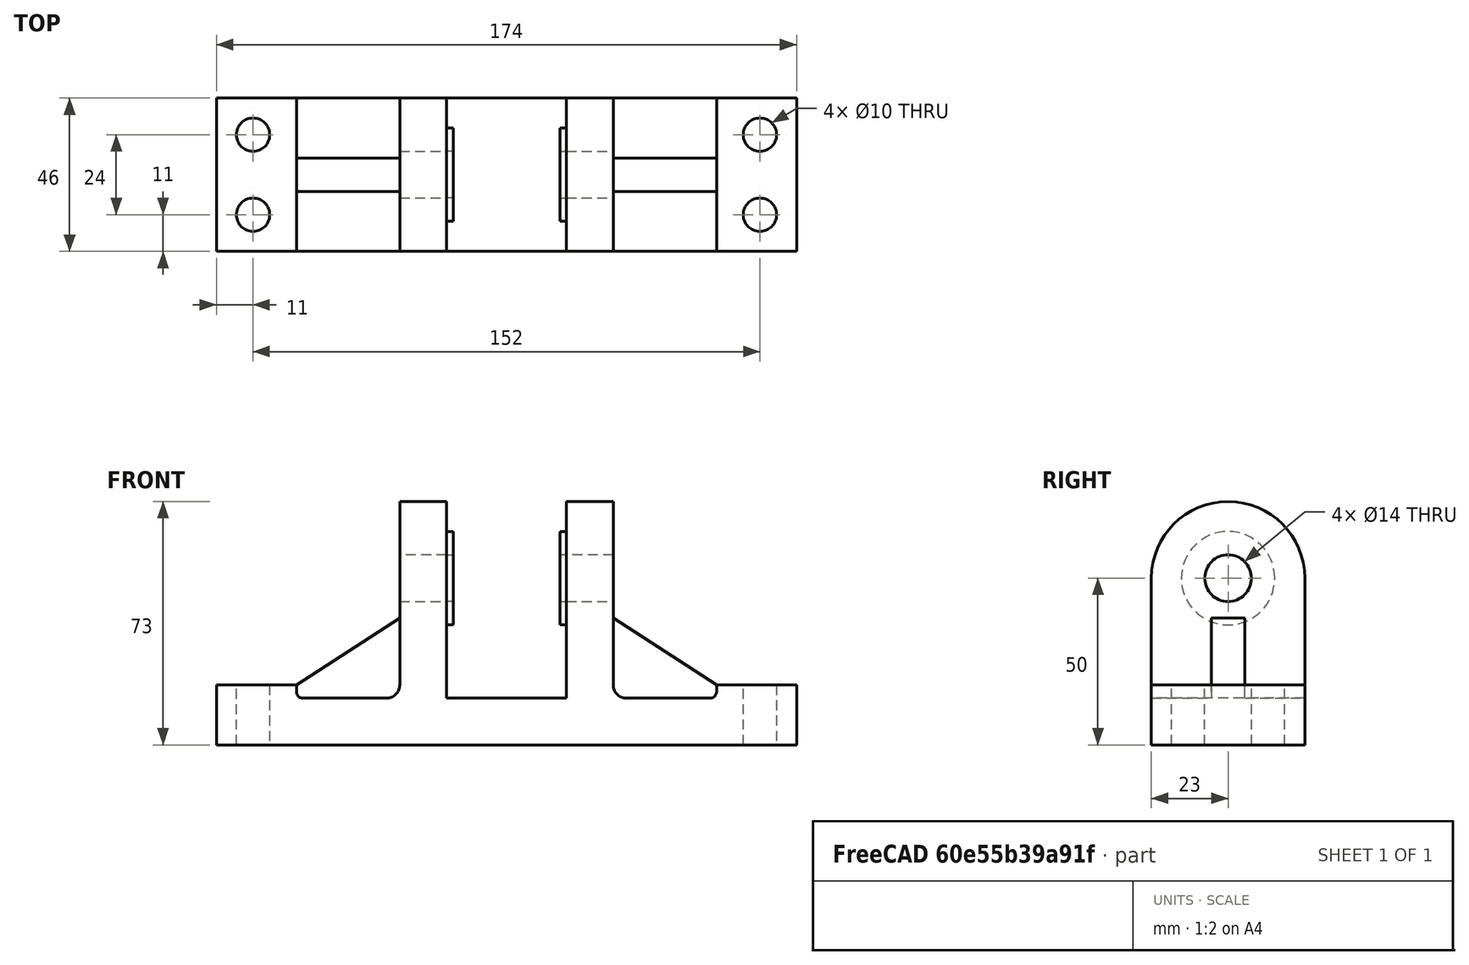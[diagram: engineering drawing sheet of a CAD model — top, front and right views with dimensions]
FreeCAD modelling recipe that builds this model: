
FCSTD DOCUMENT  (FreeCAD 0.21R33771 (Git))
Label: item_04_part_01
License: All rights reserved
LicenseURL: http://en.wikipedia.org/wiki/All_rights_reserved
objects: TechDraw::DrawViewDimension×17, Sketcher::SketchObject×9, PartDesign::Pad×5, PartDesign::Pocket×4, TechDraw::DrawProjGroupItem×3, PartDesign::Mirrored×2, PartDesign::Fillet×2, PartDesign::Body×1, TechDraw::DrawSVGTemplate×1, TechDraw::DrawViewPart×1, TechDraw::DrawProjGroup×1, TechDraw::DrawPage×1
note: 58 computed .brp shape members not serialized (recipe doc carries the construction recipe); baked Part::Feature solids carry a one-line shape summary decoded from their .brp

FEATURE [Sketcher::SketchObject] Sketch
  FullyConstrained = true
  MapMode = 5
  Placement = pos=(0,0,0) rot=(1,0,0;1.5708rad)
  Support = -> [XZ_Plane]
  sketch-geometry (5):
    g0: LineSegment StartX=-87 StartY=9 StartZ=0 EndX=-87 EndY=-9 EndZ=0
    g1: LineSegment StartX=-87 StartY=-9 StartZ=0 EndX=87 EndY=-9 EndZ=0
    g2: LineSegment StartX=87 StartY=-9 StartZ=0 EndX=87 EndY=9 EndZ=0
    g3: LineSegment StartX=87 StartY=9 StartZ=0 EndX=-87 EndY=9 EndZ=0
    g4: GeomPoint X=0 Y=0 Z=0
  constraints (12):
    c: Coincident(g0,g1)
    c: Coincident(g1,g2)
    c: Coincident(g2,g3)
    c: Coincident(g3,g0)
    c: Horizontal(g1)
    c: Horizontal(g3)
    c: Vertical(g0)
    c: Vertical(g2)
    c: Symmetric(g1,g0,g4)
    c: Coincident(g4,g-1)
    c: DistanceX(g3,g3) = 174
    c: DistanceY(g0,g0) = 18
FEATURE [PartDesign::Pad] Pad
  Direction = (0,-1,2e-16)
  Length = 46
  Length2 = 10
  Midplane = true
  Placement = pos=(0,0,0) rot=(1,0,0;1.5708rad)
  Profile = -> Sketch
  ReferenceAxis = -> Sketch [N_Axis]
  Type = 0
FEATURE [Sketcher::SketchObject] Sketch001
  ExternalGeometry = -> [Pad]
  FullyConstrained = false
  MapMode = 5
  Placement = pos=(0,0,0) rot=(1,0,0;1.5708rad)
  Support = -> [XZ_Plane]
  sketch-geometry (4):
    g0: LineSegment StartX=-63 StartY=5 StartZ=0 EndX=63 EndY=5 EndZ=0
    g1: LineSegment StartX=63 StartY=5 StartZ=0 EndX=63 EndY=36.0342 EndZ=0
    g2: LineSegment StartX=63 StartY=36.0342 StartZ=0 EndX=-63 EndY=36.0342 EndZ=0
    g3: LineSegment StartX=-63 StartY=36.0342 StartZ=0 EndX=-63 EndY=5 EndZ=0
  constraints (11):
    c: Coincident(g0,g1)
    c: Coincident(g1,g2)
    c: Coincident(g2,g3)
    c: Coincident(g3,g0)
    c: Horizontal(g0)
    c: Horizontal(g2)
    c: Vertical(g1)
    c: Vertical(g3)
    c: DistanceX(g2,g2) = 126
    c: DistanceX(g-3,g0) = 24
    c: DistanceY(g0,g-3) = 4
FEATURE [PartDesign::Pocket] Pocket
  AlongSketchNormal = false
  BaseFeature = -> Pad
  Direction = (0,1,-2e-16)
  Length = 50
  Length2 = 5
  Midplane = true
  Placement = pos=(0,0,0) rot=(1,0,0;1.5708rad)
  Profile = -> Sketch001
  ReferenceAxis = -> Sketch001 [N_Axis]
  Type = 0
FEATURE [Sketcher::SketchObject] Sketch002
  ExternalGeometry = -> [Pocket]
  FullyConstrained = true
  MapMode = 5
  Placement = pos=(0,0,0) rot=(1,0,0;1.5708rad)
  Support = -> [XZ_Plane]
  sketch-geometry (4):
    g0: LineSegment StartX=-32 StartY=-9 StartZ=0 EndX=-18 EndY=-9 EndZ=0
    g1: LineSegment StartX=-18 StartY=-9 StartZ=0 EndX=-18 EndY=64 EndZ=0
    g2: LineSegment StartX=-18 StartY=64 StartZ=0 EndX=-32 EndY=64 EndZ=0
    g3: LineSegment StartX=-32 StartY=64 StartZ=0 EndX=-32 EndY=-9 EndZ=0
  constraints (12):
    c: Coincident(g0,g1)
    c: Coincident(g1,g2)
    c: Coincident(g2,g3)
    c: Coincident(g3,g0)
    c: Horizontal(g0)
    c: Horizontal(g2)
    c: Vertical(g1)
    c: Vertical(g3)
    c: DistanceX(g-4,g0) = 55
    c: DistanceX(g2,g2) = 14
    c: DistanceY(g1,g1) = 73
    c: PointOnObject(g-6,g0)
FEATURE [PartDesign::Pad] Pad001
  BaseFeature = -> Pocket
  Direction = (0,-1,2e-16)
  Length = 46
  Length2 = 10
  Midplane = true
  Placement = pos=(0,0,0) rot=(1,0,0;1.5708rad)
  Profile = -> Sketch002
  ReferenceAxis = -> Sketch002 [N_Axis]
  Refine = true
  Type = 0
FEATURE [Sketcher::SketchObject] Sketch003
  ExternalGeometry = -> [Pad001]
  FullyConstrained = false
  MapMode = 5
  Placement = pos=(0,0,0) rot=(1,0,0;1.5708rad)
  Support = -> [XZ_Plane]
  sketch-geometry (4):
    g0: LineSegment StartX=18 StartY=-9 StartZ=0 EndX=32 EndY=-9 EndZ=0
    g1: LineSegment StartX=32 StartY=-9 StartZ=0 EndX=32 EndY=64 EndZ=0
    g2: LineSegment StartX=32 StartY=64 StartZ=0 EndX=18 EndY=64 EndZ=0
    g3: LineSegment StartX=18 StartY=64 StartZ=0 EndX=18 EndY=-9 EndZ=0
  constraints (10):
    c: Coincident(g0,g1)
    c: Coincident(g1,g2)
    c: Coincident(g2,g3)
    c: Coincident(g3,g0)
    c: Horizontal(g0)
    c: Horizontal(g2)
    c: Vertical(g1)
    c: Vertical(g3)
    c: DistanceX(g2,g2) = 14
    c: DistanceY(g1,g1) = 73
FEATURE [PartDesign::Pad] Pad002
  BaseFeature = -> Pad001
  Direction = (0,-1,2e-16)
  Length = 46
  Length2 = 10
  Midplane = true
  Placement = pos=(0,0,0) rot=(1,0,0;1.5708rad)
  Profile = -> Sketch003
  ReferenceAxis = -> Sketch003 [N_Axis]
  Refine = true
  Type = 0
FEATURE [Sketcher::SketchObject] Sketch004
  ExternalGeometry = -> [Pad002]
  FullyConstrained = true
  MapMode = 5
  Support = -> [XY_Plane]
  sketch-geometry (4):
    g0: Circle CenterX=-76 CenterY=12 CenterZ=0 NormalX=0 NormalY=0 NormalZ=1 AngleXU=0 Radius=5
    g1: Circle CenterX=-76 CenterY=-12 CenterZ=0 NormalX=0 NormalY=0 NormalZ=1 AngleXU=0 Radius=5
    g2: Circle CenterX=76 CenterY=12 CenterZ=0 NormalX=0 NormalY=0 NormalZ=1 AngleXU=0 Radius=5
    g3: Circle CenterX=76 CenterY=-12 CenterZ=0 NormalX=0 NormalY=0 NormalZ=1 AngleXU=0 Radius=5
  constraints (12):
    c: Equal(g0,g1)
    c: Equal(g1,g3)
    c: Equal(g3,g2)
    c: Diameter(g0) = 10
    c: Vertical(g0,g1)
    c: Vertical(g2,g3)
    c: Horizontal(g2,g0)
    c: Horizontal(g1,g3)
    c: DistanceY(g0,g-4) = 11
    c: DistanceX(g-4,g0) = 11
    c: DistanceY(g-6,g3) = 11
    c: DistanceX(g3,g-6) = 11
FEATURE [PartDesign::Pocket] Pocket001
  BaseFeature = -> Pad002
  Direction = (0,0,-1)
  Length = 5
  Length2 = 5
  Midplane = true
  Placement = pos=(0,0,0) rot=(1,0,0;1.5708rad)
  Profile = -> Sketch004
  ReferenceAxis = -> Sketch004 [N_Axis]
  Type = 1
FEATURE [Sketcher::SketchObject] Sketch005
  ExternalGeometry = -> [Pocket001]
  FullyConstrained = false
  MapMode = 5
  Placement = pos=(0,0,0) rot=(0.57735,0.57735,0.57735;2.0944rad)
  Support = -> [YZ_Plane]
  sketch-geometry (4):
    g0: ArcOfCircle CenterX=0 CenterY=41 CenterZ=0 NormalX=0 NormalY=0 NormalZ=1 AngleXU=0 Radius=23 StartAngle=1e-16 EndAngle=3.14159
    g1: LineSegment StartX=-23 StartY=64 StartZ=0 EndX=23 EndY=64 EndZ=0
    g2: LineSegment StartX=23 StartY=64 StartZ=0 EndX=23 EndY=41 EndZ=0
    g3: LineSegment StartX=-23 StartY=41 StartZ=0 EndX=-23 EndY=64 EndZ=0
  constraints (10):
    c: PointOnObject(g0,g-2)
    c: Diameter(g0) = 46
    c: DistanceY(g-3,g0) = 50
    c: Coincident(g1,g2)
    c: Coincident(g3,g1)
    c: Horizontal(g1)
    c: Vertical(g2)
    c: Vertical(g3)
    c: Coincident(g1,g-6)
    c: PointOnObject(g-5,g2)
FEATURE [PartDesign::Pocket] Pocket002
  BaseFeature = -> Pocket001
  Direction = (-1,2e-16,-3e-16)
  Length = 5
  Length2 = 5
  Midplane = true
  Placement = pos=(0,0,0) rot=(1,0,0;1.5708rad)
  Profile = -> Sketch005
  ReferenceAxis = -> Sketch005 [N_Axis]
  Type = 1
FEATURE [Sketcher::SketchObject] Sketch006
  ExternalGeometry = -> [Pocket002]
  FullyConstrained = true
  MapMode = 5
  Placement = pos=(32,0,0) rot=(0.707107,0,0.707107;3.14159rad)
  Support = -> [Pocket002]
  sketch-geometry (1):
    g0: Circle CenterX=41 CenterY=0 CenterZ=0 NormalX=0 NormalY=0 NormalZ=1 AngleXU=0 Radius=7
  constraints (3):
    c: DistanceX(g-3,g0) = 50
    c: PointOnObject(g0,g-1)
    c: Diameter(g0) = 14
FEATURE [PartDesign::Pocket] Pocket003
  BaseFeature = -> Pocket002
  Direction = (-1,0,2e-16)
  Length = 5
  Length2 = 5
  Placement = pos=(0,0,0) rot=(1,0,0;1.5708rad)
  Profile = -> Sketch006
  ReferenceAxis = -> Sketch006 [N_Axis]
  Type = 1
FEATURE [Sketcher::SketchObject] Sketch007
  ExternalGeometry = -> [Pocket003]
  FullyConstrained = true
  MapMode = 5
  Placement = pos=(-18,0,0) rot=(0.707107,0,0.707107;3.14159rad)
  Support = -> [Pocket003]
  sketch-geometry (2):
    g0: Circle CenterX=41 CenterY=0 CenterZ=0 NormalX=0 NormalY=0 NormalZ=1 AngleXU=0 Radius=7
    g1: Circle CenterX=41 CenterY=0 CenterZ=0 NormalX=0 NormalY=0 NormalZ=1 AngleXU=0 Radius=14
  constraints (5):
    c: PointOnObject(g0,g-1)
    c: Coincident(g1,g0)
    c: Diameter(g0) = 14
    c: Diameter(g1) = 28
    c: DistanceX(g-3,g0) = 50
FEATURE [PartDesign::Pad] Pad003
  BaseFeature = -> Pocket003
  Direction = (1,0,-2e-16)
  Length = 2
  Length2 = 10
  Placement = pos=(0,0,0) rot=(1,0,0;1.5708rad)
  Profile = -> Sketch007
  ReferenceAxis = -> Sketch007 [N_Axis]
  Type = 0
FEATURE [PartDesign::Mirrored] Mirrored
  BaseFeature = -> Pad003
  MirrorPlane = -> YZ_Plane
  Originals = -> [Pad003]
  Placement = pos=(0,0,0) rot=(1,0,0;1.5708rad)
FEATURE [Sketcher::SketchObject] Sketch008
  ExternalGeometry = -> [Mirrored]
  FullyConstrained = true
  MapMode = 5
  Placement = pos=(0,0,0) rot=(1,0,0;1.5708rad)
  Support = -> [XZ_Plane]
  sketch-geometry (4):
    g0: LineSegment StartX=32 StartY=29 StartZ=0 EndX=32 EndY=5 EndZ=0
    g1: LineSegment StartX=32 StartY=5 StartZ=0 EndX=63 EndY=5 EndZ=0
    g2: LineSegment StartX=63 StartY=5 StartZ=0 EndX=63 EndY=9 EndZ=0
    g3: LineSegment StartX=63 StartY=9 StartZ=0 EndX=32 EndY=29 EndZ=0
  constraints (9):
    c: Coincident(g0,g-4)
    c: Coincident(g0,g1)
    c: Coincident(g1,g-6)
    c: PointOnObject(g0,g-4)
    c: DistanceY(g0,g-5) = 12
    c: Coincident(g1,g2)
    c: Coincident(g2,g-7)
    c: Coincident(g2,g3)
    c: Coincident(g3,g0)
FEATURE [PartDesign::Pad] Pad004
  BaseFeature = -> Mirrored
  Direction = (0,-1,2e-16)
  Length = 10
  Length2 = 10
  Midplane = true
  Placement = pos=(0,0,0) rot=(1,0,0;1.5708rad)
  Profile = -> Sketch008
  ReferenceAxis = -> Sketch008 [N_Axis]
  Type = 0
FEATURE [PartDesign::Mirrored] Mirrored001
  BaseFeature = -> Pad004
  MirrorPlane = -> Sketch008 [V_Axis]
  Originals = -> [Pad004]
  Placement = pos=(0,0,0) rot=(1,0,0;1.5708rad)
FEATURE [PartDesign::Fillet] Fillet
  Base = -> Mirrored001 [Edge68,Edge64,Edge87,Edge84]
  BaseFeature = -> Mirrored001
  Placement = pos=(0,0,0) rot=(1,0,0;1.5708rad)
  Radius = 4
  SupportTransform = false
  UseAllEdges = false
FEATURE [PartDesign::Fillet] Fillet001
  Base = -> Fillet [Edge70,Edge108,Edge99,Edge20]
  BaseFeature = -> Fillet
  Placement = pos=(0,0,0) rot=(1,0,0;1.5708rad)
  Radius = 2
  SupportTransform = false
  UseAllEdges = false
FEATURE [PartDesign::Body] Body
  Group = -> [Sketch,Pad,Sketch001,Pocket,Sketch002,Pad001,Sketch003,Pad002,Sketch004,Pocket001,Sketch005,Pocket002,Sketch006,Pocket003,Sketch007,Pad003,Mirrored,Sketch008,Pad004,Mirrored001,Fillet,Fillet001]
  Origin = -> Origin
  Tip = -> Fillet001
FEATURE [TechDraw::DrawSVGTemplate] Template
  EditableTexts = Designed_by_Name=Reza Heshmati; Drawing_number=Drawing number; FC-Date=Date; FC-SC=Scale; FC-SH=Sheet; FC-Title=Item #4 (part 1); Subtitle=Subtitle; Weight=Weight
  Height = 210
  Orientation = 1
  Template = <path>
  Width = 297
FEATURE [TechDraw::DrawViewPart] View
  Caption = 3D View
  CoarseView = false
  Direction = (0.57735,-0.57735,0.57735)
  Focus = 100
  HardHidden = false
  IsoCount = 0
  IsoHidden = false
  IsoVisible = false
  LockPosition = false
  Perspective = false
  Rotation = 0
  Scale = 0.5
  ScaleType = 2
  ScrubCount = 0
  SeamHidden = false
  SeamVisible = false
  SmoothHidden = false
  SmoothVisible = true
  Source = -> [Fillet001]
  X = 74.4732
  XDirection = (0.707107,0.707107,0)
  Y = 153.079
FEATURE [TechDraw::DrawProjGroupItem] ProjItem  label="Side View"
  Caption = Side View
  CoarseView = false
  Direction = (0,-1,0)
  Focus = 100
  HardHidden = false
  IsoCount = 0
  IsoHidden = false
  IsoVisible = false
  LockPosition = true
  Perspective = false
  Rotation = 0
  RotationVector = (1,0,0)
  Scale = 0.5
  ScaleType = 2
  ScrubCount = 0
  SeamHidden = false
  SeamVisible = false
  SmoothHidden = false
  SmoothVisible = true
  Source = -> [Fillet001]
  Type = 0
  X = 0
  XDirection = (1,0,0)
  Y = 0
FEATURE [TechDraw::DrawProjGroupItem] ProjItem001  label="Front View"
  Caption = Front View
  CoarseView = false
  Direction = (1,-1e-16,0)
  Focus = 100
  HardHidden = false
  IsoCount = 0
  IsoHidden = false
  IsoVisible = false
  LockPosition = false
  Perspective = false
  Rotation = 0
  RotationVector = (1,0,0)
  Scale = 0.5
  ScaleType = 2
  ScrubCount = 0
  SeamHidden = false
  SeamVisible = false
  SmoothHidden = false
  SmoothVisible = true
  Source = -> [Fillet001]
  Type = 2
  X = -85
  XDirection = (1e-16,1,0)
  Y = 0
FEATURE [TechDraw::DrawProjGroupItem] ProjItem002  label="Bottom View"
  Caption = Bottom View
  CoarseView = false
  Direction = (0,0,-1)
  Focus = 100
  HardHidden = false
  IsoCount = 0
  IsoHidden = false
  IsoVisible = false
  LockPosition = false
  Perspective = false
  Rotation = 0
  RotationVector = (1,0,0)
  Scale = 0.5
  ScaleType = 2
  ScrubCount = 0
  SeamHidden = false
  SeamVisible = false
  SmoothHidden = false
  SmoothVisible = true
  Source = -> [Fillet001]
  Type = 5
  X = 0
  XDirection = (1,0,0)
  Y = 59.75
FEATURE [TechDraw::DrawProjGroup] ProjGroup
  Anchor = -> ProjItem
  AutoDistribute = true
  LockPosition = false
  ProjectionType = 0
  Rotation = 0
  Scale = 0.5
  ScaleType = 2
  Source = -> [Fillet001]
  Views = -> [ProjItem,ProjItem001,ProjItem002]
  X = 229.554
  Y = 102.7
  spacingX = 30
  spacingY = 30
FEATURE [TechDraw::DrawViewDimension] Dimension
  AngleOverride = false
  Arbitrary = false
  ArbitraryTolerances = false
  EqualTolerance = true
  ExtensionAngle = 0
  FormatSpec = %.2w
  FormatSpecOverTolerance = %+.2w
  FormatSpecUnderTolerance = %+.2w
  Inverted = false
  LineAngle = 0
  LockPosition = false
  MeasureType = 1
  OverTolerance = 0
  References2D = -> [ProjItem002]
  Rotation = 0
  ScaleType = 0
  TheoreticalExact = false
  Type = 1
  UnderTolerance = 0
  X = -2.66466
  Y = 20.5985
FEATURE [TechDraw::DrawViewDimension] Dimension001
  AngleOverride = false
  Arbitrary = false
  ArbitraryTolerances = false
  EqualTolerance = true
  ExtensionAngle = 0
  FormatSpec = %.2w
  FormatSpecOverTolerance = %+.2w
  FormatSpecUnderTolerance = %+.2w
  Inverted = false
  LineAngle = 0
  LockPosition = false
  MeasureType = 1
  OverTolerance = 0
  References2D = -> [ProjItem002]
  Rotation = 0
  ScaleType = 0
  TheoreticalExact = false
  Type = 2
  UnderTolerance = 0
  X = -49.9839
  Y = 4.40907
FEATURE [TechDraw::DrawViewDimension] Dimension002
  AngleOverride = false
  Arbitrary = false
  ArbitraryTolerances = false
  EqualTolerance = true
  ExtensionAngle = 0
  FormatSpec = %.2w
  FormatSpecOverTolerance = %+.2w
  FormatSpecUnderTolerance = %+.2w
  Inverted = false
  LineAngle = 0
  LockPosition = false
  MeasureType = 1
  OverTolerance = 0
  References2D = -> [ProjItem002]
  Rotation = 0
  ScaleType = 0
  TheoreticalExact = false
  Type = 1
  UnderTolerance = 0
  X = -40.2104
  Y = 26.6122
FEATURE [TechDraw::DrawViewDimension] Dimension003
  AngleOverride = false
  Arbitrary = false
  ArbitraryTolerances = false
  EqualTolerance = true
  ExtensionAngle = 0
  FormatSpec = %.2w
  FormatSpecOverTolerance = %+.2w
  FormatSpecUnderTolerance = %+.2w
  Inverted = false
  LineAngle = 0
  LockPosition = false
  MeasureType = 1
  OverTolerance = 0
  References2D = -> [ProjItem002]
  Rotation = 0
  ScaleType = 0
  TheoreticalExact = false
  Type = 2
  UnderTolerance = 0
  X = -57.8571
  Y = 10.8249
FEATURE [TechDraw::DrawViewDimension] Dimension004
  AngleOverride = false
  Arbitrary = false
  ArbitraryTolerances = false
  EqualTolerance = true
  ExtensionAngle = 0
  FormatSpec = %.2w
  FormatSpecOverTolerance = %+.2w
  FormatSpecUnderTolerance = %+.2w
  Inverted = false
  LineAngle = 0
  LockPosition = false
  MeasureType = 1
  OverTolerance = 0
  References2D = -> [ProjItem001]
  Rotation = 0
  ScaleType = 0
  TheoreticalExact = false
  Type = 2
  UnderTolerance = 0
  X = -27.944
  Y = -3.59525
FEATURE [TechDraw::DrawViewDimension] Dimension005
  AngleOverride = false
  Arbitrary = false
  ArbitraryTolerances = false
  EqualTolerance = true
  ExtensionAngle = 0
  FormatSpec = %.2w
  FormatSpecOverTolerance = %+.2w
  FormatSpecUnderTolerance = %+.2w
  Inverted = false
  LineAngle = 0
  LockPosition = false
  MeasureType = 1
  OverTolerance = 0
  References2D = -> [ProjItem001]
  Rotation = 0
  ScaleType = 0
  TheoreticalExact = false
  Type = 2
  UnderTolerance = 0
  X = -37.3785
  Y = -2.24805
FEATURE [TechDraw::DrawViewDimension] Dimension006
  AngleOverride = false
  Arbitrary = false
  ArbitraryTolerances = false
  EqualTolerance = true
  ExtensionAngle = 0
  FormatSpec = %.2w
  FormatSpecOverTolerance = %+.2w
  FormatSpecUnderTolerance = %+.2w
  Inverted = false
  LineAngle = 0
  LockPosition = false
  MeasureType = 1
  OverTolerance = 0
  References2D = -> [ProjItem001]
  Rotation = 0
  ScaleType = 0
  TheoreticalExact = false
  Type = 2
  UnderTolerance = 0
  X = -18.1413
  Y = -10.6665
FEATURE [TechDraw::DrawViewDimension] Dimension007
  AngleOverride = false
  Arbitrary = false
  ArbitraryTolerances = false
  EqualTolerance = true
  ExtensionAngle = 0
  FormatSpec = %.2w
  FormatSpecOverTolerance = %+.2w
  FormatSpecUnderTolerance = %+.2w
  Inverted = false
  LineAngle = 0
  LockPosition = false
  MeasureType = 1
  OverTolerance = 0
  References2D = -> [ProjItem001]
  Rotation = 0
  ScaleType = 0
  TheoreticalExact = false
  Type = 1
  UnderTolerance = 0
  X = -0.573397
  Y = 29.7901
FEATURE [TechDraw::DrawViewDimension] Dimension008
  AngleOverride = false
  Arbitrary = false
  ArbitraryTolerances = false
  EqualTolerance = true
  ExtensionAngle = 0
  FormatSpec = ⌀%.2w
  FormatSpecOverTolerance = %+.2w
  FormatSpecUnderTolerance = %+.2w
  Inverted = false
  LineAngle = 0
  LockPosition = false
  MeasureType = 1
  OverTolerance = 0
  References2D = -> [ProjItem001]
  Rotation = 0
  ScaleType = 0
  TheoreticalExact = false
  Type = 5
  UnderTolerance = 0
  X = 16.5277
  Y = 22.1754
FEATURE [TechDraw::DrawViewDimension] Dimension009
  AngleOverride = false
  Arbitrary = false
  ArbitraryTolerances = false
  EqualTolerance = true
  ExtensionAngle = 0
  FormatSpec = %.2w
  FormatSpecOverTolerance = %+.2w
  FormatSpecUnderTolerance = %+.2w
  Inverted = false
  LineAngle = 0
  LockPosition = false
  MeasureType = 1
  OverTolerance = 0
  References2D = -> [ProjItem]
  Rotation = 0
  ScaleType = 0
  TheoreticalExact = false
  Type = 2
  UnderTolerance = 0
  X = 2.27671
  Y = 9.62653
FEATURE [TechDraw::DrawViewDimension] Dimension010
  AngleOverride = false
  Arbitrary = false
  ArbitraryTolerances = false
  EqualTolerance = true
  ExtensionAngle = 0
  FormatSpec = %.2w
  FormatSpecOverTolerance = %+.2w
  FormatSpecUnderTolerance = %+.2w
  Inverted = false
  LineAngle = 0
  LockPosition = false
  MeasureType = 1
  OverTolerance = 0
  References2D = -> [ProjItem]
  Rotation = 0
  ScaleType = 0
  TheoreticalExact = false
  Type = 1
  UnderTolerance = 0
  X = -8.66781
  Y = 31.0172
FEATURE [TechDraw::DrawViewDimension] Dimension011
  AngleOverride = false
  Arbitrary = false
  ArbitraryTolerances = false
  EqualTolerance = true
  ExtensionAngle = 0
  FormatSpec = %.2w
  FormatSpecOverTolerance = %+.2w
  FormatSpecUnderTolerance = %+.2w
  Inverted = false
  LineAngle = 0
  LockPosition = false
  MeasureType = 1
  OverTolerance = 0
  References2D = -> [ProjItem]
  Rotation = 0
  ScaleType = 0
  TheoreticalExact = false
  Type = 1
  UnderTolerance = 0
  X = 12.7223
  Y = 29.4186
FEATURE [TechDraw::DrawViewDimension] Dimension012
  AngleOverride = false
  Arbitrary = false
  ArbitraryTolerances = false
  EqualTolerance = true
  ExtensionAngle = 0
  FormatSpec = %.2w
  FormatSpecOverTolerance = %+.2w
  FormatSpecUnderTolerance = %+.2w
  Inverted = false
  LineAngle = 0
  LockPosition = false
  MeasureType = 1
  OverTolerance = 0
  References2D = -> [ProjItem]
  Rotation = 0
  ScaleType = 0
  TheoreticalExact = false
  Type = 1
  UnderTolerance = 0
  X = 28.0534
  Y = 10.2781
FEATURE [TechDraw::DrawViewDimension] Dimension013
  AngleOverride = false
  Arbitrary = false
  ArbitraryTolerances = false
  EqualTolerance = true
  ExtensionAngle = 0
  FormatSpec = %.2w
  FormatSpecOverTolerance = %+.2w
  FormatSpecUnderTolerance = %+.2w
  Inverted = false
  LineAngle = 0
  LockPosition = false
  MeasureType = 1
  OverTolerance = 0
  References2D = -> [ProjItem]
  Rotation = 0
  ScaleType = 0
  TheoreticalExact = false
  Type = 1
  UnderTolerance = 0
  X = 37.2214
  Y = 0.400882
FEATURE [TechDraw::DrawViewDimension] Dimension014
  AngleOverride = false
  Arbitrary = false
  ArbitraryTolerances = false
  EqualTolerance = true
  ExtensionAngle = 0
  FormatSpec = %.2w
  FormatSpecOverTolerance = %+.2w
  FormatSpecUnderTolerance = %+.2w
  Inverted = false
  LineAngle = 0
  LockPosition = false
  MeasureType = 1
  OverTolerance = 0
  References2D = -> [ProjItem]
  Rotation = 0
  ScaleType = 0
  TheoreticalExact = false
  Type = 2
  UnderTolerance = 0
  X = -51.2175
  Y = -12.2082
FEATURE [TechDraw::DrawViewDimension] Dimension015
  AngleOverride = false
  Arbitrary = false
  ArbitraryTolerances = false
  EqualTolerance = true
  ExtensionAngle = 0
  FormatSpec = ⌀%.2w
  FormatSpecOverTolerance = %+.2w
  FormatSpecUnderTolerance = %+.2w
  Inverted = false
  LineAngle = 0
  LockPosition = false
  MeasureType = 1
  OverTolerance = 0
  References2D = -> [ProjItem]
  Rotation = 0
  ScaleType = 0
  TheoreticalExact = false
  Type = 5
  UnderTolerance = 0
  X = -30.6266
  Y = 8.41029
FEATURE [TechDraw::DrawViewDimension] Dimension017
  AngleOverride = false
  Arbitrary = false
  ArbitraryTolerances = false
  EqualTolerance = true
  ExtensionAngle = 0
  FormatSpec = ⌀%.2w
  FormatSpecOverTolerance = %+.2w
  FormatSpecUnderTolerance = %+.2w
  Inverted = false
  LineAngle = 0
  LockPosition = false
  MeasureType = 1
  OverTolerance = 0
  References2D = -> [ProjItem]
  Rotation = 0
  ScaleType = 0
  TheoreticalExact = false
  Type = 5
  UnderTolerance = 0
  X = 26.502
  Y = -0.084671
FEATURE [TechDraw::DrawPage] Page
  KeepUpdated = true
  NextBalloonIndex = 1
  ProjectionType = 0
  Template = -> Template
  Views = -> [View,ProjGroup,Dimension,Dimension001,Dimension002,Dimension003,Dimension004,Dimension005,Dimension006,Dimension007,Dimension008,Dimension009,Dimension010,Dimension011,Dimension012,Dimension013,Dimension014,Dimension015,Dimension017]
note: 1 file-system path scrubbed to <path> (originals preserved in the JSON sidecar)
